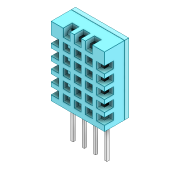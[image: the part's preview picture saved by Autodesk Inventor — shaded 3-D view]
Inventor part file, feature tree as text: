
AUTODESK INVENTOR PART (.ipt)
format: ipt  version: 2021 (Build 250183000, 183)  size: 442,368 bytes
history: native  units: mm
features: other x10, fillet x2
ambient origin geometry x8: Origin, YZ Plane, XZ Plane, XY Plane, X Axis, Y Axis, Z Axis, Center Point
bodies: Body1 (feature_tree), Body2 (feature_tree), Body3 (feature_tree), Body4 (feature_tree), Body5 (feature_tree), Body6 (feature_tree)
feature tree (12):
  other  "Твердое тело1"
  other  "Твердое тело2"
  other  "Твердое тело3"
  other  "Твердое тело4"
  other  "Твердое тело5"
  other  "Твердое тело6"
  fillet  "Fillet1"  [1 undecoded]
  other  "Cut-Extrude5[2]"
  other  "Cut-Extrude5[3]"
  other  "Cut-Extrude5[4]"
  other  "Cut-Extrude5[5]"
  fillet  "Fillet3"  [1 undecoded]
note: 2 required parameter values undecoded (feature->parameter linkage not recoverable at this tier; creation-order binding heuristic only, values carry confidence <= 0.55)
